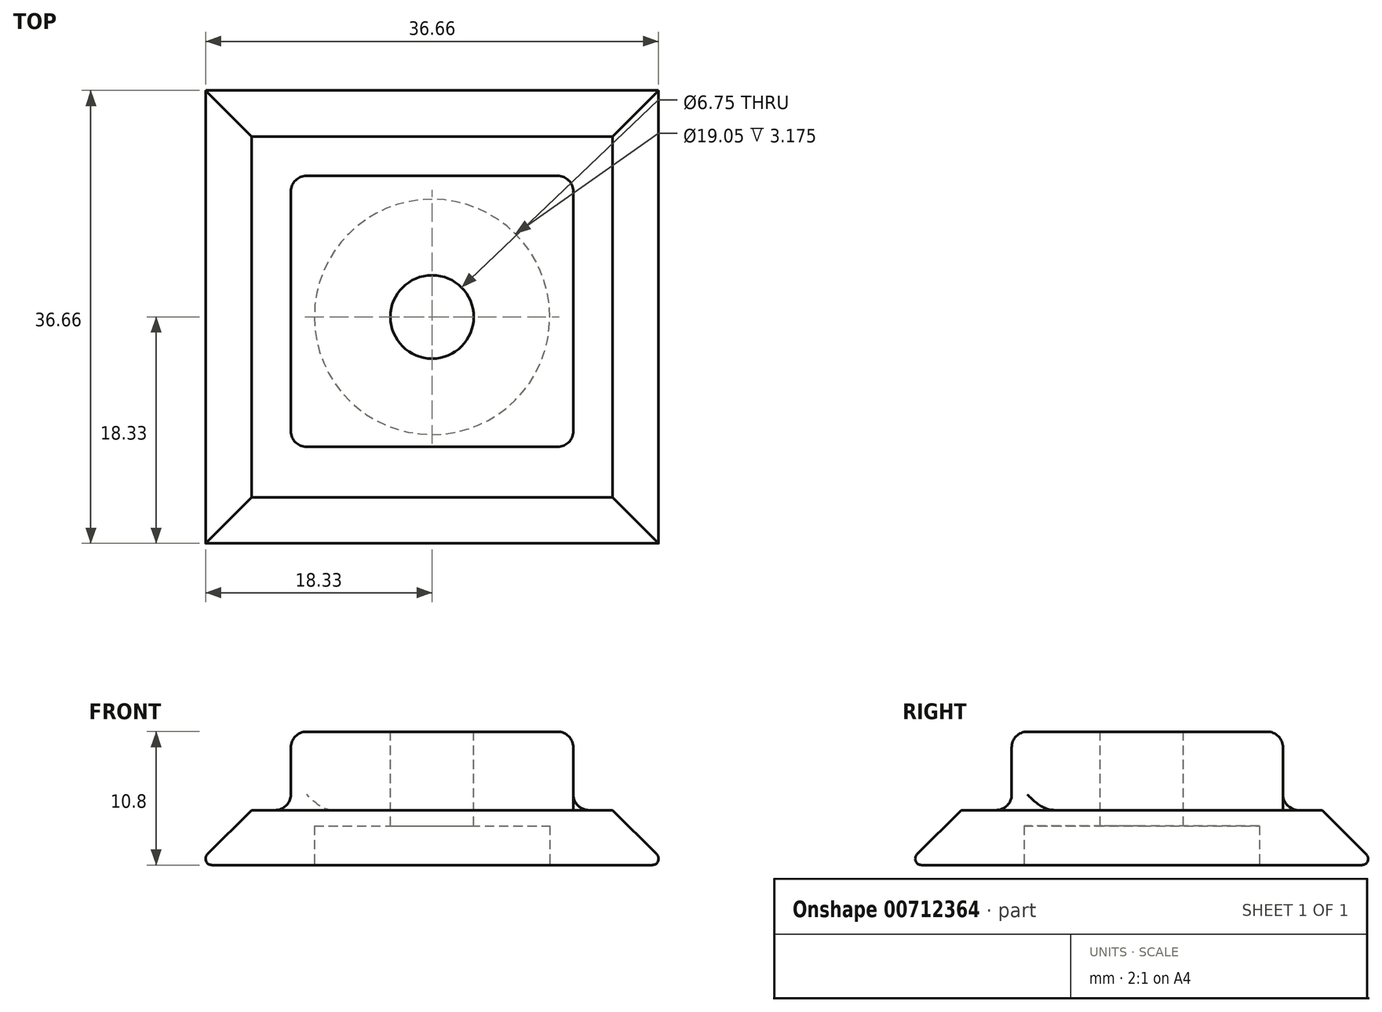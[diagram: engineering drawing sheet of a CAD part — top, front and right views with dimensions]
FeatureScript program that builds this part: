
annotation { "Feature Type Name" : "Feature", "Feature Type Description" : "" }
export const myFeature = defineFeature(function(context is Context, id is Id, definition is map)
    precondition{}
    {
        {
            var Q0;
            Q0=qCreatedBy(makeId("Top.planeOp"),FACE);
            var sketch = newSketch(context, id + "F0", { "sketchPlane" : qUnion([Q0])});
            skLineSegment(sketch, "E0.bottom", {"start": v(19.05, -19.05) * mm, "end": v(-19.05, -19.05) * mm});
            skLineSegment(sketch, "E0.top", {"start": v(19.05, 19.05) * mm, "end": v(-19.05, 19.05) * mm});
            skLineSegment(sketch, "E0.left", {"start": v(19.05, -19.05) * mm, "end": v(19.05, 19.05) * mm});
            skLineSegment(sketch, "E0.right", {"start": v(-19.05, -19.05) * mm, "end": v(-19.05, 19.05) * mm});
            skPoint(sketch, "E0.middle", {"position": v(0, 0) * mm});
            skSolve(sketch);
        }
        {
            var Q0;
            Q0 = qSketchRegion(id + "F0", true);
            extrude(context, id + "F1", {"entities" : qUnion([Q0]), "depth" : 4.44 * mm, "offsetDistance" : 25.4 * mm});
        }
        {
            var Q0;
            Q0=makeQuery(id+"F1.opExtrude","SWEPT_FACE",FACE,{"disambiguationData":[OSD([sQuery(id+"F0.wireOp",EDGE,"E0.bottom")])]});
            var sketch = newSketch(context, id + "F2", { "sketchPlane" : qUnion([Q0])});
            skLineSegment(sketch, "E1", {"start": v(-19.05, 0) * mm, "end": v(-14.6, 4.44) * mm});
            skLineSegment(sketch, "E2", {"start": v(-14.6, 4.45) * mm, "end": v(-19.05, 4.45) * mm});
            skLineSegment(sketch, "E3", {"start": v(-19.05, 4.45) * mm, "end": v(-19.05, 0) * mm});
            skLineSegment(sketch, "E4", {"start": v(0, 0.26) * mm, "end": v(0, 5.97) * mm, "construction": true});
            skPoint(sketch, "E4.endSnap0", {"position": v(0, 4.45) * mm});
            skLineSegment(sketch, "E5.MirrorCS", {"start": v(19.05, 0) * mm, "end": v(14.6, 4.45) * mm});
            skLineSegment(sketch, "E6.MirrorCS", {"start": v(19.05, 4.45) * mm, "end": v(19.05, 0) * mm});
            skLineSegment(sketch, "E7.MirrorCS", {"start": v(14.6, 4.45) * mm, "end": v(19.05, 4.45) * mm});
            skSolve(sketch);
        }
        {
            var Q0;
            Q0=makeQuery(id+"F1.opExtrude","SWEPT_FACE",FACE,{"disambiguationData":[OSD([sQuery(id+"F0.wireOp",EDGE,"E0.right")])]});
            var sketch = newSketch(context, id + "F3", { "sketchPlane" : qUnion([Q0])});
            skLineSegment(sketch, "E8", {"start": v(-19.05, 0) * mm, "end": v(-14.6, 4.45) * mm});
            skLineSegment(sketch, "E9", {"start": v(-14.6, 4.45) * mm, "end": v(-19.05, 4.45) * mm});
            skLineSegment(sketch, "E10", {"start": v(-19.05, 4.45) * mm, "end": v(-19.05, 0) * mm});
            skLineSegment(sketch, "E11", {"start": v(0, 0) * mm, "end": v(0, 6.1) * mm, "construction": true});
            skLineSegment(sketch, "E12.MirrorCS", {"start": v(19.05, 0) * mm, "end": v(14.6, 4.45) * mm});
            skLineSegment(sketch, "E13.MirrorCS", {"start": v(19.05, 4.45) * mm, "end": v(19.05, 0) * mm});
            skLineSegment(sketch, "E14.MirrorCS", {"start": v(14.6, 4.45) * mm, "end": v(19.05, 4.45) * mm});
            skSolve(sketch);
        }
        {
            var Q0;
            Q0 = qSketchRegion(id + "F2", true);
            extrude(context, id + "F4", {"entities" : qUnion([Q0]), "operationType" : NewBodyOperationType.REMOVE, "endBound" : BoundingType.THROUGH_ALL, "oppositeDirection" : true, "depth" : 25.4 * mm, "offsetDistance" : 25.4 * mm});
        }
        {
            var Q0;
            Q0 = qSketchRegion(id + "F3", true);
            extrude(context, id + "F5", {"entities" : qUnion([Q0]), "operationType" : NewBodyOperationType.REMOVE, "endBound" : BoundingType.THROUGH_ALL, "oppositeDirection" : true, "depth" : 25.4 * mm, "offsetDistance" : 25.4 * mm});
        }
        {
            var Q0;
            Q0=makeQuery(id+"F4.boolean.opBoolean","MERGE",EDGE,{"derivedFrom":[makeQuery(id+"F1.opExtrude","CAP_EDGE",EDGE,{"disambiguationData":[OSD([sQuery(id+"F0.wireOp",EDGE,"E0.left")])],"isStart":true}),makeQuery(id+"F4.opExtrude","SWEPT_EDGE",EDGE,{"disambiguationData":[OSD([sQuery(id+"F0.wireOp",EDGE,"E0.bottom"),sQuery(id+"F2.wireOp",EDGE,"E5.MirrorCS"),sQuery(id+"F2.wireOp",EDGE,"E6.MirrorCS")])]})]});
            var Q1;
            Q1=makeQuery(id+"F5.boolean.opBoolean","MERGE",EDGE,{"derivedFrom":[makeQuery(id+"F1.opExtrude","CAP_EDGE",EDGE,{"disambiguationData":[OSD([sQuery(id+"F0.wireOp",EDGE,"E0.bottom")])],"isStart":true}),makeQuery(id+"F5.opExtrude","SWEPT_EDGE",EDGE,{"disambiguationData":[OSD([sQuery(id+"F0.wireOp",EDGE,"E0.right"),sQuery(id+"F3.wireOp",EDGE,"E12.MirrorCS"),sQuery(id+"F3.wireOp",EDGE,"E13.MirrorCS")])]})]});
            var Q2;
            Q2=makeQuery(id+"F4.boolean.opBoolean","MERGE",EDGE,{"derivedFrom":[makeQuery(id+"F1.opExtrude","CAP_EDGE",EDGE,{"disambiguationData":[OSD([sQuery(id+"F0.wireOp",EDGE,"E0.right")])],"isStart":true}),makeQuery(id+"F4.opExtrude","SWEPT_EDGE",EDGE,{"disambiguationData":[OSD([sQuery(id+"F0.wireOp",EDGE,"E0.bottom"),sQuery(id+"F2.wireOp",EDGE,"E1"),sQuery(id+"F2.wireOp",EDGE,"E3")])]})]});
            var Q3;
            Q3=makeQuery(id+"F5.boolean.opBoolean","MERGE",EDGE,{"derivedFrom":[makeQuery(id+"F1.opExtrude","CAP_EDGE",EDGE,{"disambiguationData":[OSD([sQuery(id+"F0.wireOp",EDGE,"E0.top")])],"isStart":true}),makeQuery(id+"F5.opExtrude","SWEPT_EDGE",EDGE,{"disambiguationData":[OSD([sQuery(id+"F0.wireOp",EDGE,"E0.right"),sQuery(id+"F3.wireOp",EDGE,"E8"),sQuery(id+"F3.wireOp",EDGE,"E10")])]})]});
            fillet(context, id + "F6", {"entities" : qUnion([Q0, Q1, Q2, Q3]), "radius" : 0.5 * mm, "tangentPropagation" : true, "allowEdgeOverflow" : false});
        }
        {
            var Q0;
            Q0=makeQuery(id+"F1.opExtrude","CAP_FACE",FACE,{"disambiguationData":[OSD([sQuery(id+"F0.wireOp",EDGE,"E0.bottom"),sQuery(id+"F0.wireOp",EDGE,"E0.top"),sQuery(id+"F0.wireOp",EDGE,"E0.left"),sQuery(id+"F0.wireOp",EDGE,"E0.right")])],"isStart":false});
            var sketch = newSketch(context, id + "F7", { "sketchPlane" : qUnion([Q0])});
            skLineSegment(sketch, "E15.bottom", {"start": v(11.43, -10.52) * mm, "end": v(-11.43, -10.52) * mm});
            skLineSegment(sketch, "E15.top", {"start": v(11.43, 11.43) * mm, "end": v(-11.43, 11.43) * mm});
            skLineSegment(sketch, "E15.left", {"start": v(11.43, -10.52) * mm, "end": v(11.43, 11.43) * mm});
            skLineSegment(sketch, "E15.right", {"start": v(-11.43, -10.52) * mm, "end": v(-11.43, 11.43) * mm});
            skPoint(sketch, "E15.middle", {"position": v(0, 0.45) * mm});
            skSolve(sketch);
        }
        {
            var Q0;
            Q0 = qSketchRegion(id + "F7", true);
            extrude(context, id + "F8", {"entities" : qUnion([Q0]), "operationType" : NewBodyOperationType.ADD, "depth" : 6.35 * mm, "offsetDistance" : 25.4 * mm});
        }
        {
            var Q0;
            Q0=makeQuery(id+"F8.opExtrude","CAP_FACE",FACE,{"disambiguationData":[OSD([sQuery(id+"F7.wireOp",EDGE,"E15.bottom"),sQuery(id+"F7.wireOp",EDGE,"E15.top"),sQuery(id+"F7.wireOp",EDGE,"E15.left"),sQuery(id+"F7.wireOp",EDGE,"E15.right")])],"isStart":false});
            var sketch = newSketch(context, id + "F9", { "sketchPlane" : qUnion([Q0])});
            skCircle(sketch, "E16", {"center": v(0, 0) * mm, "radius": 3.37 * mm});
            skSolve(sketch);
        }
        {
            var Q0;
            Q0 = qSketchRegion(id + "F9", true);
            extrude(context, id + "F10", {"entities" : qUnion([Q0]), "operationType" : NewBodyOperationType.REMOVE, "endBound" : BoundingType.THROUGH_ALL, "oppositeDirection" : true, "depth" : 25.4 * mm, "offsetDistance" : 25.4 * mm});
        }
        {
            var Q0;
            Q0=makeQuery(id+"F1.opExtrude","CAP_FACE",FACE,{"disambiguationData":[OSD([sQuery(id+"F0.wireOp",EDGE,"E0.bottom"),sQuery(id+"F0.wireOp",EDGE,"E0.top"),sQuery(id+"F0.wireOp",EDGE,"E0.left"),sQuery(id+"F0.wireOp",EDGE,"E0.right")])],"isStart":true});
            var sketch = newSketch(context, id + "F11", { "sketchPlane" : qUnion([Q0])});
            skCircle(sketch, "E17", {"center": v(0, 0) * mm, "radius": 9.53 * mm});
            skSolve(sketch);
        }
        {
            var Q0;
            Q0 = qSketchRegion(id + "F11", true);
            extrude(context, id + "F12", {"entities" : qUnion([Q0]), "operationType" : NewBodyOperationType.REMOVE, "oppositeDirection" : true, "depth" : 3.17 * mm, "offsetDistance" : 25.4 * mm});
        }
        {
            var Q0;
            Q0=makeQuery(id+"F8.opExtrude","CAP_EDGE",EDGE,{"disambiguationData":[OSD([sQuery(id+"F7.wireOp",EDGE,"E15.right")])],"isStart":true});
            var Q1;
            Q1=makeQuery(id+"F8.opExtrude","CAP_EDGE",EDGE,{"disambiguationData":[OSD([sQuery(id+"F7.wireOp",EDGE,"E15.bottom")])],"isStart":true});
            var Q2;
            Q2=makeQuery(id+"F8.opExtrude","SWEPT_EDGE",EDGE,{"disambiguationData":[OSD([sQuery(id+"F7.wireOp",EDGE,"E15.bottom"),sQuery(id+"F7.wireOp",EDGE,"E15.right")])]});
            var Q3;
            Q3=makeQuery(id+"F8.opExtrude","SWEPT_EDGE",EDGE,{"disambiguationData":[OSD([sQuery(id+"F7.wireOp",EDGE,"E15.top"),sQuery(id+"F7.wireOp",EDGE,"E15.right")])]});
            var Q4;
            Q4=makeQuery(id+"F8.opExtrude","SWEPT_EDGE",EDGE,{"disambiguationData":[OSD([sQuery(id+"F7.wireOp",EDGE,"E15.top"),sQuery(id+"F7.wireOp",EDGE,"E15.left")])]});
            var Q5;
            Q5=makeQuery(id+"F8.opExtrude","SWEPT_EDGE",EDGE,{"disambiguationData":[OSD([sQuery(id+"F7.wireOp",EDGE,"E15.bottom"),sQuery(id+"F7.wireOp",EDGE,"E15.left")])]});
            var Q6;
            Q6=makeQuery(id+"F8.opExtrude","CAP_EDGE",EDGE,{"disambiguationData":[OSD([sQuery(id+"F7.wireOp",EDGE,"E15.top")])],"isStart":false});
            var Q7;
            Q7=makeQuery(id+"F8.opExtrude","CAP_EDGE",EDGE,{"disambiguationData":[OSD([sQuery(id+"F7.wireOp",EDGE,"E15.left")])],"isStart":false});
            var Q8;
            Q8=makeQuery(id+"F8.opExtrude","CAP_EDGE",EDGE,{"disambiguationData":[OSD([sQuery(id+"F7.wireOp",EDGE,"E15.bottom")])],"isStart":false});
            var Q9;
            {var subQ0=sQuery(id+"F2.wireOp",EDGE,"E1");Q9=makeQuery(id+"F6.opFillet","BLEND_EDGE",EDGE,{"blendedFrom":[makeQuery(id+"F4.boolean.opBoolean","MERGE",EDGE,{"derivedFrom":[makeQuery(id+"F1.opExtrude","CAP_EDGE",EDGE,{"disambiguationData":[OSD([sQuery(id+"F0.wireOp",EDGE,"E0.right")])],"isStart":true}),makeQuery(id+"F4.opExtrude","SWEPT_EDGE",EDGE,{"disambiguationData":[OSD([sQuery(id+"F0.wireOp",EDGE,"E0.bottom"),subQ0,sQuery(id+"F2.wireOp",EDGE,"E3")])]})]}),makeQuery(id+"F4.boolean.opBoolean","COPY",FACE,{"derivedFrom":makeQuery(id+"F4.opExtrude","SWEPT_FACE",FACE,{"disambiguationData":[OSD([subQ0])]})})],"blendedInto":[makeQuery(id+"F4.boolean.opBoolean","COPY",FACE,{"derivedFrom":makeQuery(id+"F4.opExtrude","SWEPT_FACE",FACE,{"disambiguationData":[OSD([subQ0])]})})]});}
            var Q10;
            Q10=makeQuery(id+"F8.opExtrude","CAP_EDGE",EDGE,{"disambiguationData":[OSD([sQuery(id+"F7.wireOp",EDGE,"E15.right")])],"isStart":false});
            fillet(context, id + "F13", {"entities" : qUnion([Q0, Q1, Q2, Q3, Q4, Q5, Q6, Q7, Q8, Q9, Q10]), "radius" : 1.27 * mm, "tangentPropagation" : true, "allowEdgeOverflow" : false});
        }
    });
